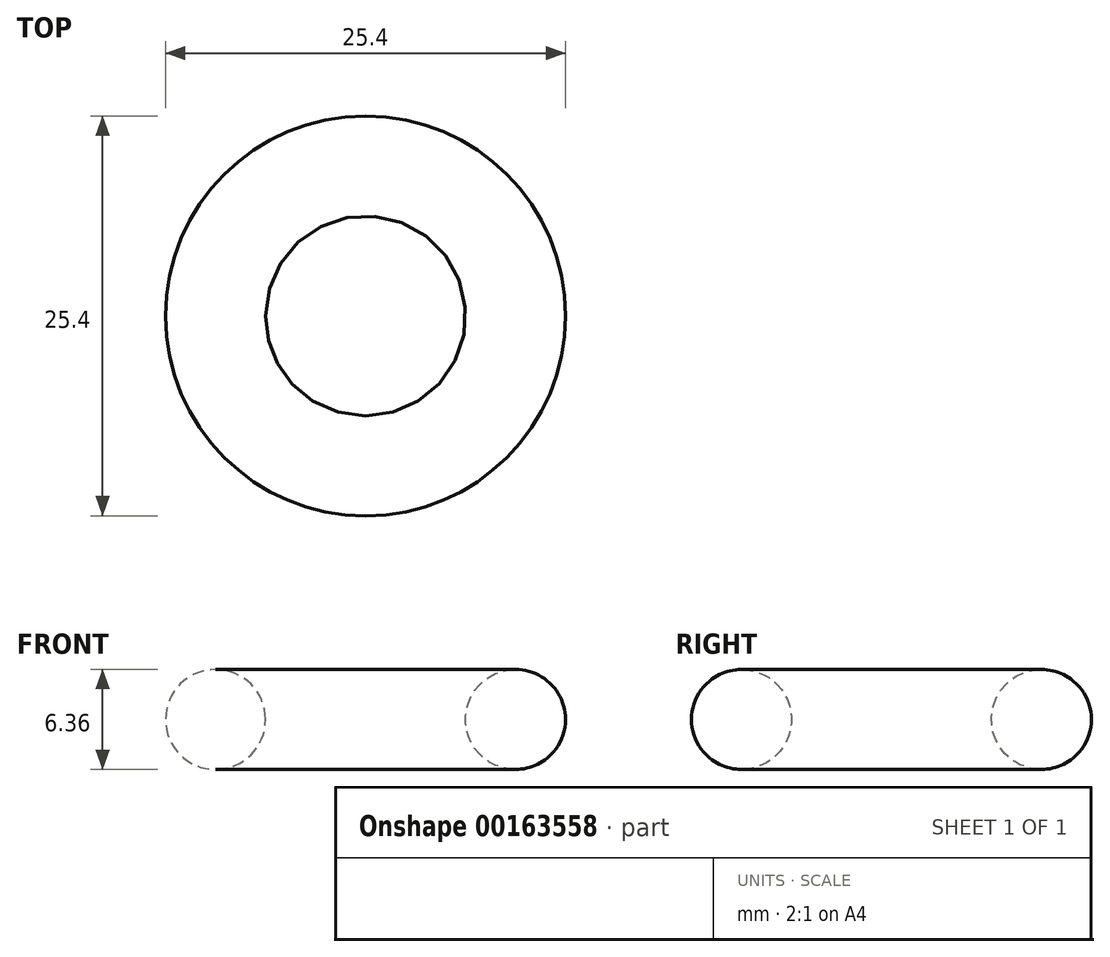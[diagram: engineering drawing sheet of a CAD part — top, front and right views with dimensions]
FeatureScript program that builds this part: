
annotation { "Feature Type Name" : "Feature", "Feature Type Description" : "" }
export const myFeature = defineFeature(function(context is Context, id is Id, definition is map)
    precondition{}
    {
        {
            var Q0;
            Q0=qCreatedBy(makeId("Front.planeOp"),FACE);
            var sketch = newSketch(context, id + "F0", { "sketchPlane" : qUnion([Q0])});
            skCircle(sketch, "E0", {"center": v(0, 0) * mm, "radius": 3.18 * mm});
            skLineSegment(sketch, "E1", {"start": v(9.53, 0) * mm, "end": v(9.53, 2.46) * mm});
            skSolve(sketch);
        }
        {
            var Q0;
            Q0=makeQuery(id+"F0.imprint","IMPRINT",FACE,{"disambiguationData":[TD([[makeQuery(id+"F0.imprint","IMPRINT",EDGE,{"derivedFrom":sQuery(id+"F0.wireOp",EDGE,"E0")}),1.0]])]});
            var Q1;
            Q1=sQuery(id+"F0.wireOp",EDGE,"E1");
            revolve(context, id + "F1", {"entities" : qUnion([Q0]), "axis" : qUnion([Q1]), "revolveType" : RevolveType.FULL});
        }
        {
            var Q0;
            Q0=makeQuery(id+"F1.opRevolve","SWEPT_BODY",BODY,{"disambiguationData":[OSD([sQuery(id+"F0.wireOp",EDGE,"E0")])]});
            transform(context, id + "F2", {"entities" : qUnion([Q0]), "transformType" : TransformType.TRANSLATION_3D, "dx" : -9.52 * mm, "dy" : 0 * mm, "dz" : 0 * mm, "makeCopy" : false});
        }
    });
